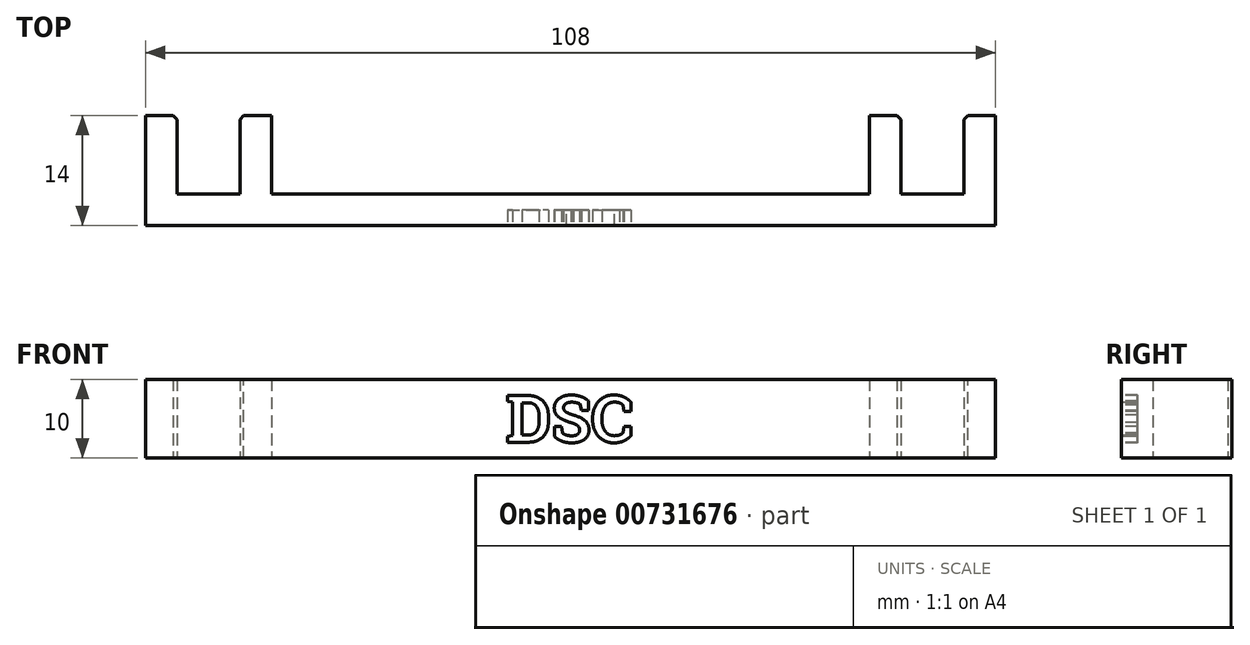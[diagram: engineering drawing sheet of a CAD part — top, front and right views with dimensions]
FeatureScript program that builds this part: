
annotation { "Feature Type Name" : "Feature", "Feature Type Description" : "" }
export const myFeature = defineFeature(function(context is Context, id is Id, definition is map)
    precondition{}
    {
        {
            var Q0;
            Q0=qCreatedBy(makeId("Top.planeOp"),FACE);
            var sketch = newSketch(context, id + "F0", { "sketchPlane" : qUnion([Q0])});
            skLineSegment(sketch, "E0", {"start": v(-54, 14) * mm, "end": v(-54, 0) * mm});
            skLineSegment(sketch, "E1", {"start": v(-54, 0) * mm, "end": v(54, 0) * mm});
            skLineSegment(sketch, "E2", {"start": v(54, 0) * mm, "end": v(54, 14) * mm});
            skLineSegment(sketch, "E3", {"start": v(54, 14) * mm, "end": v(50, 14) * mm});
            skLineSegment(sketch, "E4", {"start": v(50, 14) * mm, "end": v(50, 4) * mm});
            skLineSegment(sketch, "E5", {"start": v(50, 4) * mm, "end": v(42, 4) * mm});
            skLineSegment(sketch, "E6", {"start": v(42, 4) * mm, "end": v(42, 14) * mm});
            skLineSegment(sketch, "E7", {"start": v(42, 14) * mm, "end": v(38, 14) * mm});
            skLineSegment(sketch, "E8", {"start": v(38, 14) * mm, "end": v(38, 4) * mm});
            skLineSegment(sketch, "E9", {"start": v(38, 4) * mm, "end": v(-38, 4) * mm});
            skLineSegment(sketch, "E10", {"start": v(-38, 4) * mm, "end": v(-38, 14) * mm});
            skLineSegment(sketch, "E11", {"start": v(-38, 14) * mm, "end": v(-42, 14) * mm});
            skLineSegment(sketch, "E12", {"start": v(-42, 14) * mm, "end": v(-42, 4) * mm});
            skLineSegment(sketch, "E13", {"start": v(-42, 4) * mm, "end": v(-50, 4) * mm});
            skLineSegment(sketch, "E14", {"start": v(-50, 4) * mm, "end": v(-50, 14) * mm});
            skLineSegment(sketch, "E15", {"start": v(-50, 14) * mm, "end": v(-54, 14) * mm});
            skSolve(sketch);
        }
        {
            var Q0;
            Q0 = qSketchRegion(id + "F0", true);
            extrude(context, id + "F1", {"entities" : qUnion([Q0]), "depth" : 10 * mm, "offsetDistance" : 25 * mm});
        }
        {
            var Q0;
            Q0=qCreatedBy(makeId("Front.planeOp"),FACE);
            var sketch = newSketch(context, id + "F2", { "sketchPlane" : qUnion([Q0])});
            skText(sketch, "E16", { "text": "DSC", "fontName": "RobotoSlab-Bold.ttf"});
            const initialGuessF2  = {"E16": [-0.0082, 0.002, 1, 0, 0.006]};
            skSetInitialGuess(sketch, initialGuessF2);
            skSolve(sketch);
        }
        {
            var Q0;
            Q0 = qSketchRegion(id + "F2", true);
            extrude(context, id + "F3", {"entities" : qUnion([Q0]), "operationType" : NewBodyOperationType.REMOVE, "oppositeDirection" : true, "depth" : 2 * mm, "offsetDistance" : 25 * mm});
        }
        {
            var Q0;
            Q0=makeQuery(id+"F1.opExtrude","SWEPT_EDGE",EDGE,{"disambiguationData":[OSD([sQuery(id+"F0.wireOp",EDGE,"E11"),sQuery(id+"F0.wireOp",EDGE,"E12")])]});
            var Q1;
            Q1=makeQuery(id+"F1.opExtrude","SWEPT_EDGE",EDGE,{"disambiguationData":[OSD([sQuery(id+"F0.wireOp",EDGE,"E14"),sQuery(id+"F0.wireOp",EDGE,"E15")])]});
            var Q2;
            Q2=makeQuery(id+"F1.opExtrude","SWEPT_EDGE",EDGE,{"disambiguationData":[OSD([sQuery(id+"F0.wireOp",EDGE,"E6"),sQuery(id+"F0.wireOp",EDGE,"E7")])]});
            var Q3;
            Q3=makeQuery(id+"F1.opExtrude","SWEPT_EDGE",EDGE,{"disambiguationData":[OSD([sQuery(id+"F0.wireOp",EDGE,"E3"),sQuery(id+"F0.wireOp",EDGE,"E4")])]});
            chamfer(context, id + "F4", {"entities" : qUnion([Q0, Q1, Q2, Q3]), "width" : 0.5 * mm, "tangentPropagation" : true});
        }
    });
